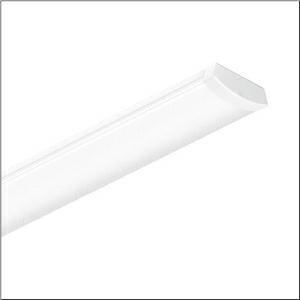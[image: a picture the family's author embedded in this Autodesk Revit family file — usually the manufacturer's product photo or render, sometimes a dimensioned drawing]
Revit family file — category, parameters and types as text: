
# Revit family: siluette_21_51ln12mkm40a
name_source: partatom
category: Lighting Fixtures
units: mm (PartAtom-declared; Revit-internal decimal feet)

## family parameters
Cut with Voids When Loaded = No
Host = Face
Light Source = No
Part Type = Normal
Room Calculation Point = No
Round Connector Dimension = Use Diameter
Shared = No

## types (1)
- --- (1 x LED, 2980 lm, 20.6 W, 5000K)
    Apparent Load = 21 VA
    CIE Flux Codes = 43 73 92 94 100
    Color Rendering = 80
    Color Temperature = 5000K
    Default Elevation = 1800 mm
    Description = Siluette 21, office luminaire, primary optical cover: enclosure, of PC, frosted, light emission: direct distribution, primary light characteristic: symmetric, installation type: suspended mounting, surface-mounted, LED, rated luminous flux: 5.010lm, luminous efficacy: 144lm/W, light colour: 830/840/850, colour temperature: 3000/4000/5000K, control gear: ON/OFF Multilumen, with terminal, 3-pole, mains connection: 220..240V, AC, 50/60Hz, rated input power: 35W, housing, of sheet steel, white, length: 1.200mm, width: 152mm, height: 53mm, end cap, of PMMA, white, protection rating (complete): IP44, insulation class (complete): insulation class I (protective earthing), certification: CE, UKCA, protection symbol: D, impact resistance: IK04, permissible operating ambient temperature: -20..+40°C, contact your sales advisor before using the luminaires in applications with unclear chemical exposure, large temperature fluctuations or condensation-forming humidity, corresponds to IFS (International Featured Standards) requirements for safety and quality in the food industry, packaging unit: 1 piece
    Height = 52 mm
    Lamp = 1 x LED
    Lamp Light Flux = 2980 lm
    Lamp Power = 20.6 W
    Lamp count = 1
    Length = 1185 mm
    Luminous efficacy = 145 lm/W
    Manufacturer = Siteco
    ModVariant = No
    Model = 51LN12MKM40A
    Mounting Place = Ceiling
    Mounting Type = Pendant
    Number of Poles = 1
    OnlyDefault = Yes
    Power Factor = 1
    Product Name = Siluette 21
    Product group = office luminaire | ceiling pendant
    ProductGroupID = 903
    Protection Class = Protection class I
    Protection Degree = IP 44
    RLX_Detail_Level = 1
    RLX_Emergency_Light_Flux = 0 lm
    RLX_Emergency_Type = 0
    RLX_Emergency_Type_DB = No
    RlxData = <blob elided: 19245 chars, md5=f0b485b0>
    Socket = socket
    Standby Power = 0 W
    System Light Flux = 2980 lm
    System Power = 21 W
    Type Comments = individual setting: colour temperature 5000K, luminous flux: 60 % | (OFF | OFF | ON) | 200 mA
    Type Image = l_1296910.jpg
    URL = http://relux.com
    VarID = @adj_065847
    Voltage = 0 V
    Weight = 0.00 kg
    Width = 152 mm

## geometry (parser evidence)
native form markers: Blend x4, Sweep x12
no freeform markers — native parametric forms only
